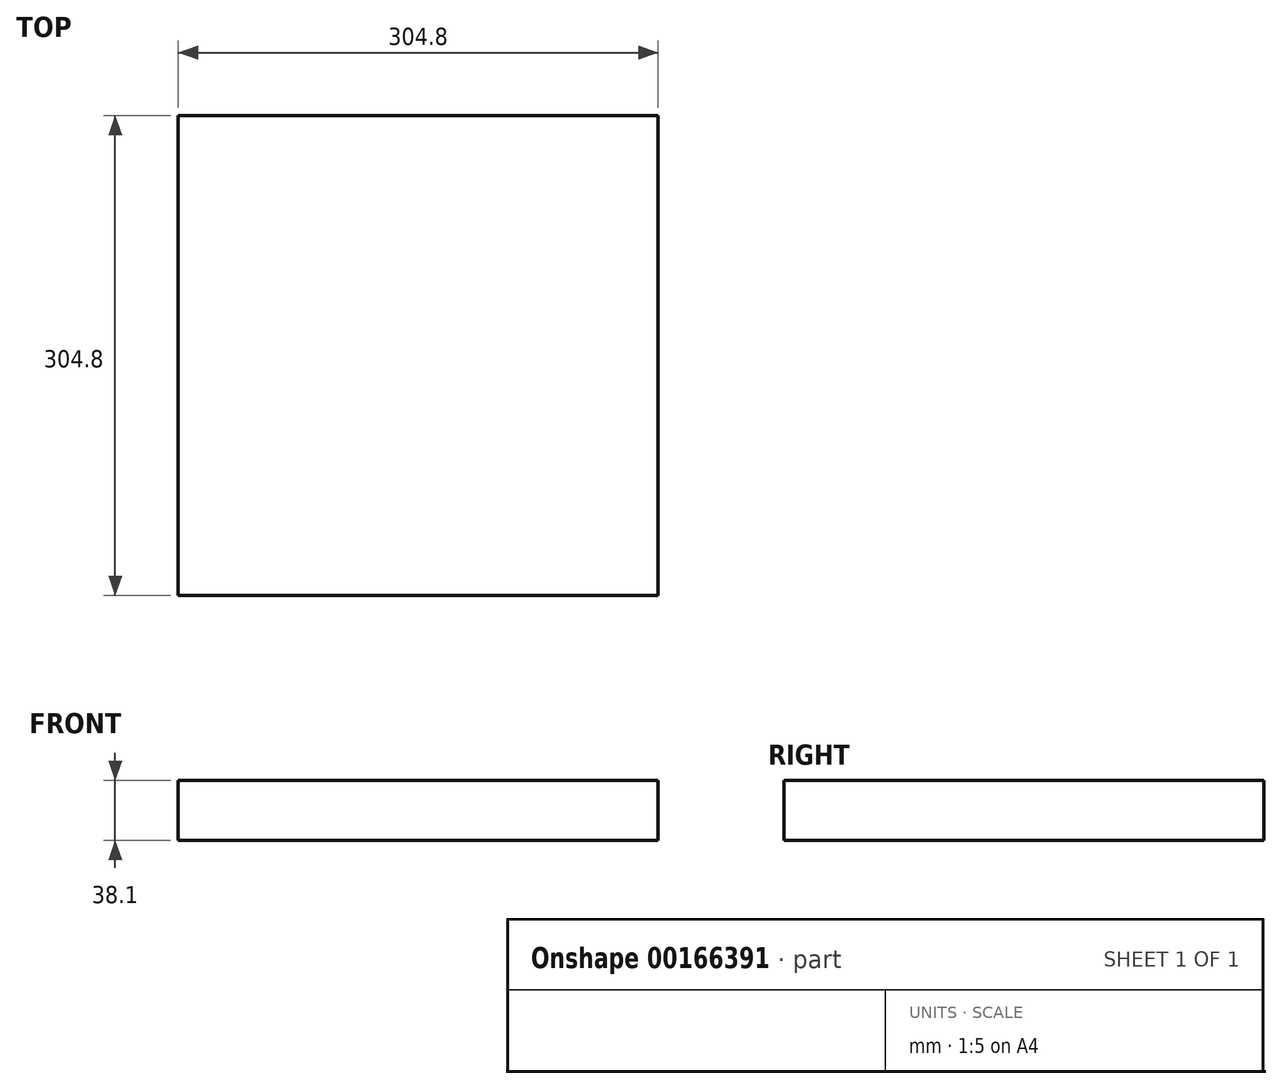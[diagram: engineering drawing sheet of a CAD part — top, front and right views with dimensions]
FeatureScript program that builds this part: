
annotation { "Feature Type Name" : "Feature", "Feature Type Description" : "" }
export const myFeature = defineFeature(function(context is Context, id is Id, definition is map)
    precondition{}
    {
        {
            var Q0;
            Q0=qCreatedBy(makeId("Top.planeOp"),FACE);
            var sketch = newSketch(context, id + "F0", { "sketchPlane" : qUnion([Q0])});
            skLineSegment(sketch, "E0.bottom", {"start": v(152.4, -152.4) * mm, "end": v(-152.4, -152.4) * mm});
            skLineSegment(sketch, "E0.top", {"start": v(152.4, 152.4) * mm, "end": v(-152.4, 152.4) * mm});
            skLineSegment(sketch, "E0.left", {"start": v(152.4, -152.4) * mm, "end": v(152.4, 152.4) * mm});
            skLineSegment(sketch, "E0.right", {"start": v(-152.4, -152.4) * mm, "end": v(-152.4, 152.4) * mm});
            skPoint(sketch, "E0.middle", {"position": v(0, 0) * mm});
            skSolve(sketch);
        }
        {
            var Q0;
            Q0=makeQuery(id+"F0.imprint","IMPRINT",FACE,{"disambiguationData":[TD([[makeQuery(id+"F0.imprint","IMPRINT",EDGE,{"derivedFrom":sQuery(id+"F0.wireOp",EDGE,"E0.bottom")}),-1.0]])]});
            extrude(context, id + "F1", {"entities" : qUnion([Q0]), "depth" : 38.1 * mm});
        }
    });
